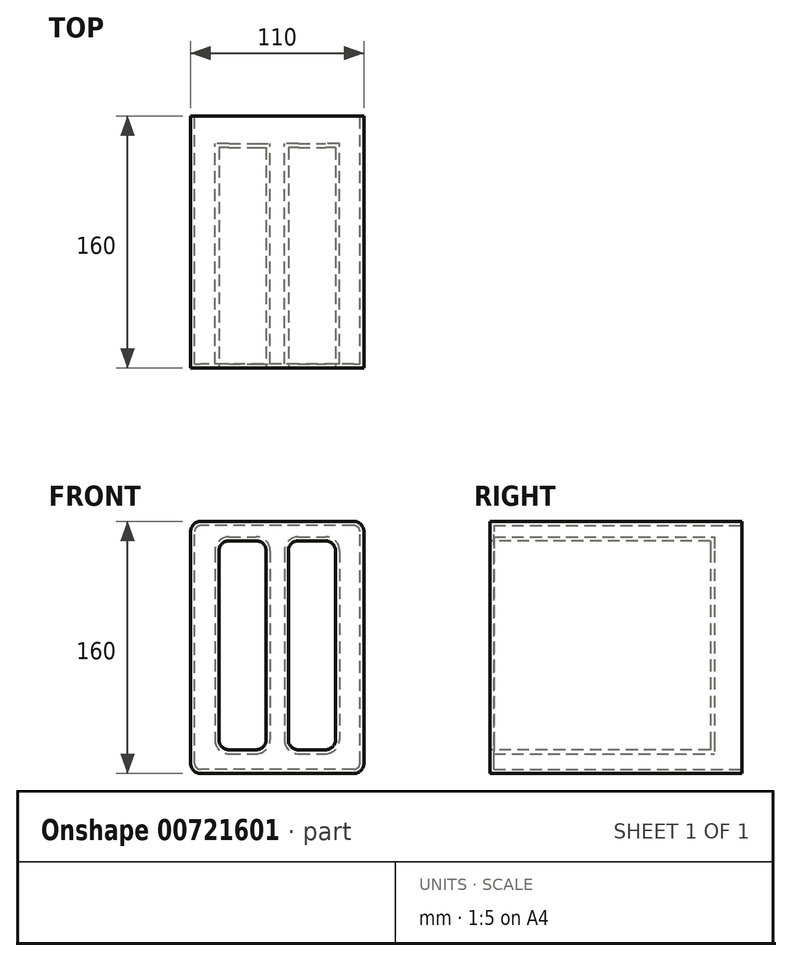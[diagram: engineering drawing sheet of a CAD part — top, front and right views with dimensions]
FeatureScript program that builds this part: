
annotation { "Feature Type Name" : "Feature", "Feature Type Description" : "" }
export const myFeature = defineFeature(function(context is Context, id is Id, definition is map)
    precondition{}
    {
        {
            var Q0;
            Q0=qCreatedBy(makeId("Front.planeOp"),FACE);
            var sketch = newSketch(context, id + "F0", { "sketchPlane" : qUnion([Q0])});
            skLineSegment(sketch, "E0.bottom", {"start": v(-6.35, 0) * mm, "end": v(-103.65, 0) * mm});
            skLineSegment(sketch, "E0.top", {"start": v(-6.35, 160) * mm, "end": v(-103.65, 160) * mm});
            skLineSegment(sketch, "E0.left", {"start": v(0, 6.35) * mm, "end": v(0, 153.65) * mm});
            skLineSegment(sketch, "E0.right", {"start": v(-110, 6.35) * mm, "end": v(-110, 153.65) * mm});
            skPoint(sketch, "E1.visualSharp", {"position": v(-110, 160) * mm});
            skArc(sketch, "E1.filletArc", {"start": v(-103.65, 160) * mm, "mid": v(-108.14, 158.14) * mm, "end": v(-110, 153.65) * mm});
            skPoint(sketch, "E2.visualSharp", {"position": v(0, 160) * mm});
            skArc(sketch, "E2.filletArc", {"start": v(0, 153.65) * mm, "mid": v(-1.86, 158.14) * mm, "end": v(-6.35, 160) * mm});
            skPoint(sketch, "E3.visualSharp", {"position": v(0, 0) * mm});
            skArc(sketch, "E3.filletArc", {"start": v(-6.35, 0) * mm, "mid": v(-1.86, 1.86) * mm, "end": v(0, 6.35) * mm});
            skPoint(sketch, "E4.visualSharp", {"position": v(-110, 0) * mm});
            skArc(sketch, "E4.filletArc", {"start": v(-110, 6.35) * mm, "mid": v(-108.14, 1.86) * mm, "end": v(-103.65, 0) * mm});
            skSolve(sketch);
        }
        {
            var Q0;
            Q0=makeQuery(id+"F0.imprint","IMPRINT",FACE,{"disambiguationData":[TD([[makeQuery(id+"F0.imprint","IMPRINT",EDGE,{"derivedFrom":sQuery(id+"F0.wireOp",EDGE,"E0.bottom")}),-1.0]])]});
            extrude(context, id + "F1", {"entities" : qUnion([Q0]), "depth" : 160 * mm, "offsetDistance" : 25.4 * mm});
        }
        {
            var Q0;
            Q0=makeQuery(id+"F1.opExtrude","CAP_FACE",FACE,{"disambiguationData":[OSD([sQuery(id+"F0.wireOp",EDGE,"E0.bottom"),sQuery(id+"F0.wireOp",EDGE,"E0.top"),sQuery(id+"F0.wireOp",EDGE,"E0.left"),sQuery(id+"F0.wireOp",EDGE,"E0.right"),sQuery(id+"F0.wireOp",EDGE,"E1.filletArc"),sQuery(id+"F0.wireOp",EDGE,"E2.filletArc"),sQuery(id+"F0.wireOp",EDGE,"E3.filletArc"),sQuery(id+"F0.wireOp",EDGE,"E4.filletArc")])],"isStart":false});
            var sketch = newSketch(context, id + "F2", { "sketchPlane" : qUnion([Q0])});
            skLineSegment(sketch, "E5.bottom", {"start": v(-85.65, 147.7) * mm, "end": v(-68.35, 147.7) * mm});
            skLineSegment(sketch, "E5.top", {"start": v(-85.65, 15) * mm, "end": v(-68.35, 15) * mm});
            skLineSegment(sketch, "E5.left", {"start": v(-92, 141.35) * mm, "end": v(-92, 21.35) * mm});
            skLineSegment(sketch, "E5.right", {"start": v(-62, 141.35) * mm, "end": v(-62, 21.35) * mm});
            skLineSegment(sketch, "E6.bottom", {"start": v(-41.65, 147.7) * mm, "end": v(-24.35, 147.7) * mm});
            skLineSegment(sketch, "E6.top", {"start": v(-41.65, 15) * mm, "end": v(-24.35, 15) * mm});
            skLineSegment(sketch, "E6.left", {"start": v(-48, 141.35) * mm, "end": v(-48, 21.35) * mm});
            skLineSegment(sketch, "E6.right", {"start": v(-18, 141.35) * mm, "end": v(-18, 21.35) * mm});
            skPoint(sketch, "E7.visualSharp", {"position": v(-62, 147.7) * mm});
            skArc(sketch, "E7.filletArc", {"start": v(-62, 141.35) * mm, "mid": v(-63.86, 145.84) * mm, "end": v(-68.35, 147.7) * mm});
            skPoint(sketch, "E8.visualSharp", {"position": v(-92, 15) * mm});
            skArc(sketch, "E8.filletArc", {"start": v(-92, 21.35) * mm, "mid": v(-90.14, 16.86) * mm, "end": v(-85.65, 15) * mm});
            skPoint(sketch, "E9.visualSharp", {"position": v(-92, 147.7) * mm});
            skArc(sketch, "E9.filletArc", {"start": v(-85.65, 147.7) * mm, "mid": v(-90.14, 145.84) * mm, "end": v(-92, 141.35) * mm});
            skPoint(sketch, "E10.visualSharp", {"position": v(-48, 147.7) * mm});
            skArc(sketch, "E10.filletArc", {"start": v(-41.65, 147.7) * mm, "mid": v(-46.14, 145.84) * mm, "end": v(-48, 141.35) * mm});
            skPoint(sketch, "E11.visualSharp", {"position": v(-18, 15) * mm});
            skArc(sketch, "E11.filletArc", {"start": v(-24.35, 15) * mm, "mid": v(-19.86, 16.86) * mm, "end": v(-18, 21.35) * mm});
            skPoint(sketch, "E12.visualSharp", {"position": v(-62, 15) * mm});
            skArc(sketch, "E12.filletArc", {"start": v(-68.35, 15) * mm, "mid": v(-63.86, 16.86) * mm, "end": v(-62, 21.35) * mm});
            skPoint(sketch, "E13.visualSharp", {"position": v(-18, 147.7) * mm});
            skArc(sketch, "E13.filletArc", {"start": v(-18, 141.35) * mm, "mid": v(-19.86, 145.84) * mm, "end": v(-24.35, 147.7) * mm});
            skPoint(sketch, "E14.visualSharp", {"position": v(-48, 15) * mm});
            skArc(sketch, "E14.filletArc", {"start": v(-48, 21.35) * mm, "mid": v(-46.14, 16.86) * mm, "end": v(-41.65, 15) * mm});
            skPoint(sketch, "E15", {"position": v(-110, 80) * mm});
            skPoint(sketch, "E16", {"position": v(-55, 160) * mm});
            skPoint(sketch, "E17", {"position": v(-55, 80) * mm});
            skSolve(sketch);
        }
        {
            var Q0;
            Q0=makeQuery(id+"F2.imprint","IMPRINT",FACE,{"disambiguationData":[TD([[makeQuery(id+"F2.imprint","IMPRINT",EDGE,{"derivedFrom":sQuery(id+"F2.wireOp",EDGE,"E6.bottom")}),-1.0]])]});
            var Q1;
            Q1=makeQuery(id+"F2.imprint","IMPRINT",FACE,{"disambiguationData":[TD([[makeQuery(id+"F2.imprint","IMPRINT",EDGE,{"derivedFrom":sQuery(id+"F2.wireOp",EDGE,"E5.bottom")}),-1.0]])]});
            extrude(context, id + "F3", {"entities" : qUnion([Q0, Q1]), "operationType" : NewBodyOperationType.REMOVE, "oppositeDirection" : true, "depth" : 140 * mm, "offsetDistance" : 25.4 * mm});
        }
        {
            var Q0;
            Q0=makeQuery(id+"F1.opExtrude","CAP_FACE",FACE,{"disambiguationData":[OSD([sQuery(id+"F0.wireOp",EDGE,"E0.bottom"),sQuery(id+"F0.wireOp",EDGE,"E0.top"),sQuery(id+"F0.wireOp",EDGE,"E0.left"),sQuery(id+"F0.wireOp",EDGE,"E0.right"),sQuery(id+"F0.wireOp",EDGE,"E1.filletArc"),sQuery(id+"F0.wireOp",EDGE,"E2.filletArc"),sQuery(id+"F0.wireOp",EDGE,"E3.filletArc"),sQuery(id+"F0.wireOp",EDGE,"E4.filletArc")])],"isStart":true});
            shell(context, id + "F4", {"entities" : qUnion([Q0]), "thickness" : 2.54 * mm});
        }
    });
